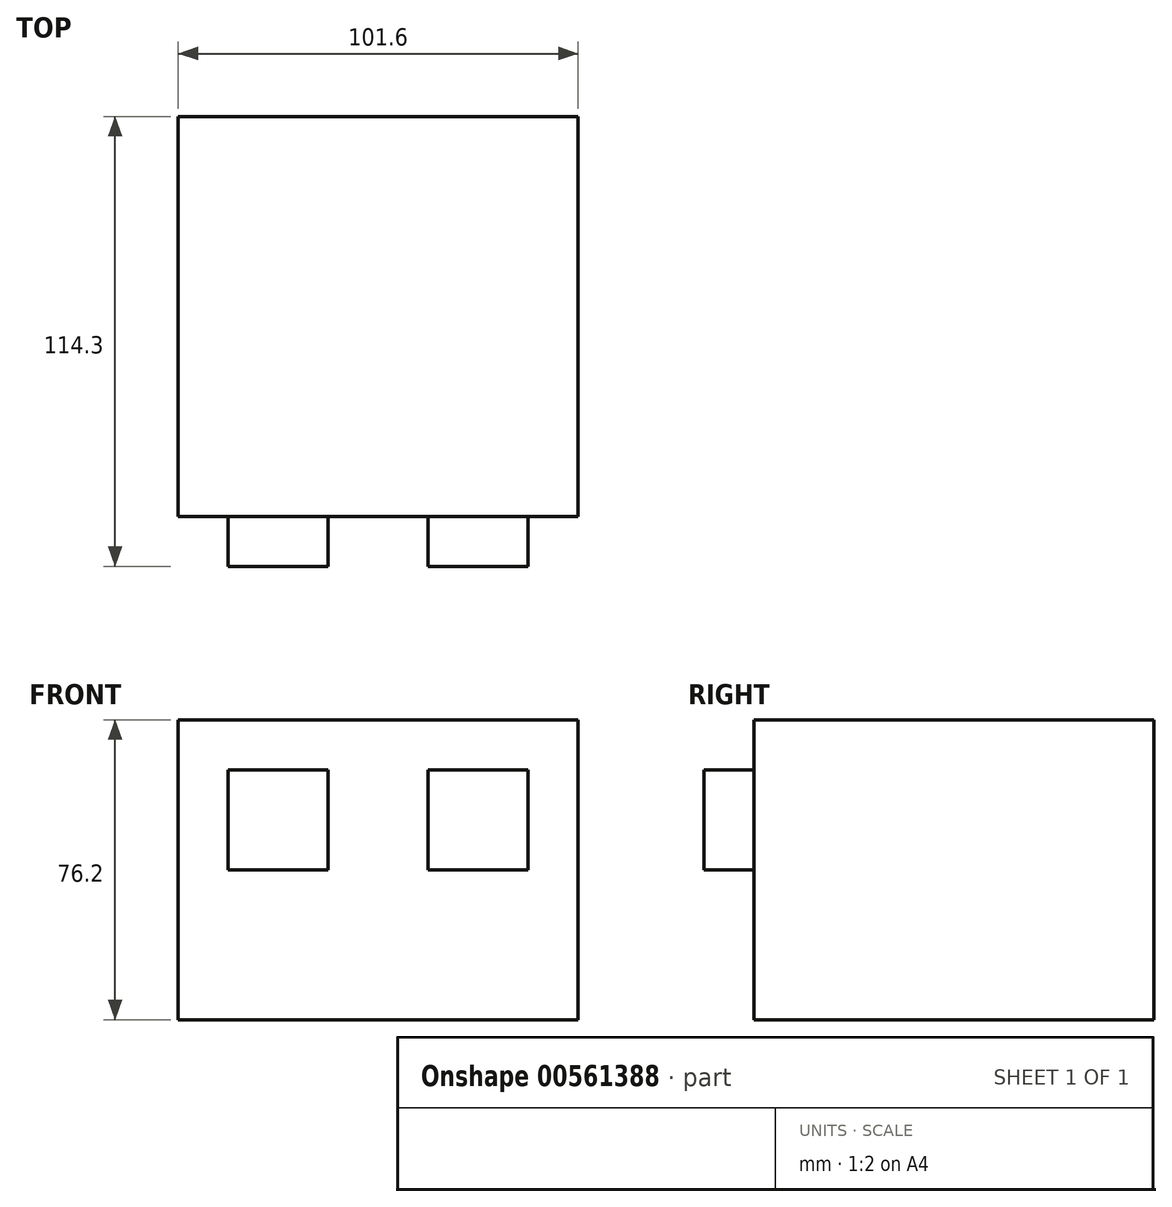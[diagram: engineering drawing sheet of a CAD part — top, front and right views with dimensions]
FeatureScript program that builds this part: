
annotation { "Feature Type Name" : "Feature", "Feature Type Description" : "" }
export const myFeature = defineFeature(function(context is Context, id is Id, definition is map)
    precondition{}
    {
        {
            var Q0;
            Q0=qCreatedBy(makeId("Front.planeOp"),FACE);
            var sketch = newSketch(context, id + "F0", { "sketchPlane" : qUnion([Q0])});
            skLineSegment(sketch, "E0.bottom", {"start": v(0, 0) * mm, "end": v(101.6, 0) * mm});
            skLineSegment(sketch, "E0.top", {"start": v(0, 76.2) * mm, "end": v(101.6, 76.2) * mm});
            skLineSegment(sketch, "E0.left", {"start": v(0, 0) * mm, "end": v(0, 76.2) * mm});
            skLineSegment(sketch, "E0.right", {"start": v(101.6, 0) * mm, "end": v(101.6, 76.2) * mm});
            skSolve(sketch);
        }
        {
            var Q0;
            Q0=makeQuery(id+"F0.imprint","IMPRINT",FACE,{"disambiguationData":[TD([[makeQuery(id+"F0.imprint","IMPRINT",EDGE,{"derivedFrom":sQuery(id+"F0.wireOp",EDGE,"E0.bottom")}),1.0]])]});
            extrude(context, id + "F1", {"entities" : qUnion([Q0]), "depth" : 101.6 * mm, "offsetDistance" : 25.4 * mm});
        }
        {
            var Q0;
            Q0=makeQuery(id+"F1.opExtrude","CAP_FACE",FACE,{"disambiguationData":[OSD([sQuery(id+"F0.wireOp",EDGE,"E0.bottom"),sQuery(id+"F0.wireOp",EDGE,"E0.top"),sQuery(id+"F0.wireOp",EDGE,"E0.left"),sQuery(id+"F0.wireOp",EDGE,"E0.right")])],"isStart":false});
            var sketch = newSketch(context, id + "F2", { "sketchPlane" : qUnion([Q0])});
            skLineSegment(sketch, "E1.bottom", {"start": v(12.7, 38.1) * mm, "end": v(38.1, 38.1) * mm});
            skLineSegment(sketch, "E1.top", {"start": v(12.7, 63.5) * mm, "end": v(38.1, 63.5) * mm});
            skLineSegment(sketch, "E1.left", {"start": v(12.7, 38.1) * mm, "end": v(12.7, 63.5) * mm});
            skLineSegment(sketch, "E1.right", {"start": v(38.1, 38.1) * mm, "end": v(38.1, 63.5) * mm});
            skSolve(sketch);
        }
        {
            var Q0;
            Q0=makeQuery(id+"F2.imprint","IMPRINT",FACE,{"disambiguationData":[TD([[makeQuery(id+"F2.imprint","IMPRINT",EDGE,{"derivedFrom":sQuery(id+"F2.wireOp",EDGE,"E1.bottom")}),1.0]])]});
            extrude(context, id + "F3", {"entities" : qUnion([Q0]), "operationType" : NewBodyOperationType.ADD, "depth" : 12.7 * mm, "offsetDistance" : 25.4 * mm});
        }
        {
            var Q0;
            Q0=makeQuery(id+"F1.opExtrude","CAP_FACE",FACE,{"disambiguationData":[OSD([sQuery(id+"F0.wireOp",EDGE,"E0.bottom"),sQuery(id+"F0.wireOp",EDGE,"E0.top"),sQuery(id+"F0.wireOp",EDGE,"E0.left"),sQuery(id+"F0.wireOp",EDGE,"E0.right")])],"isStart":false});
            var sketch = newSketch(context, id + "F4", { "sketchPlane" : qUnion([Q0])});
            skLineSegment(sketch, "E2.bottom", {"start": v(63.5, 38.1) * mm, "end": v(88.9, 38.1) * mm});
            skLineSegment(sketch, "E2.top", {"start": v(63.5, 63.5) * mm, "end": v(88.9, 63.5) * mm});
            skLineSegment(sketch, "E2.left", {"start": v(63.5, 38.1) * mm, "end": v(63.5, 63.5) * mm});
            skLineSegment(sketch, "E2.right", {"start": v(88.9, 38.1) * mm, "end": v(88.9, 63.5) * mm});
            skSolve(sketch);
        }
        {
            var Q0;
            Q0=makeQuery(id+"F4.imprint","IMPRINT",FACE,{"disambiguationData":[TD([[makeQuery(id+"F4.imprint","IMPRINT",EDGE,{"derivedFrom":sQuery(id+"F4.wireOp",EDGE,"E2.bottom")}),1.0]])]});
            extrude(context, id + "F5", {"entities" : qUnion([Q0]), "operationType" : NewBodyOperationType.ADD, "depth" : 12.7 * mm, "offsetDistance" : 25.4 * mm});
        }
    });
